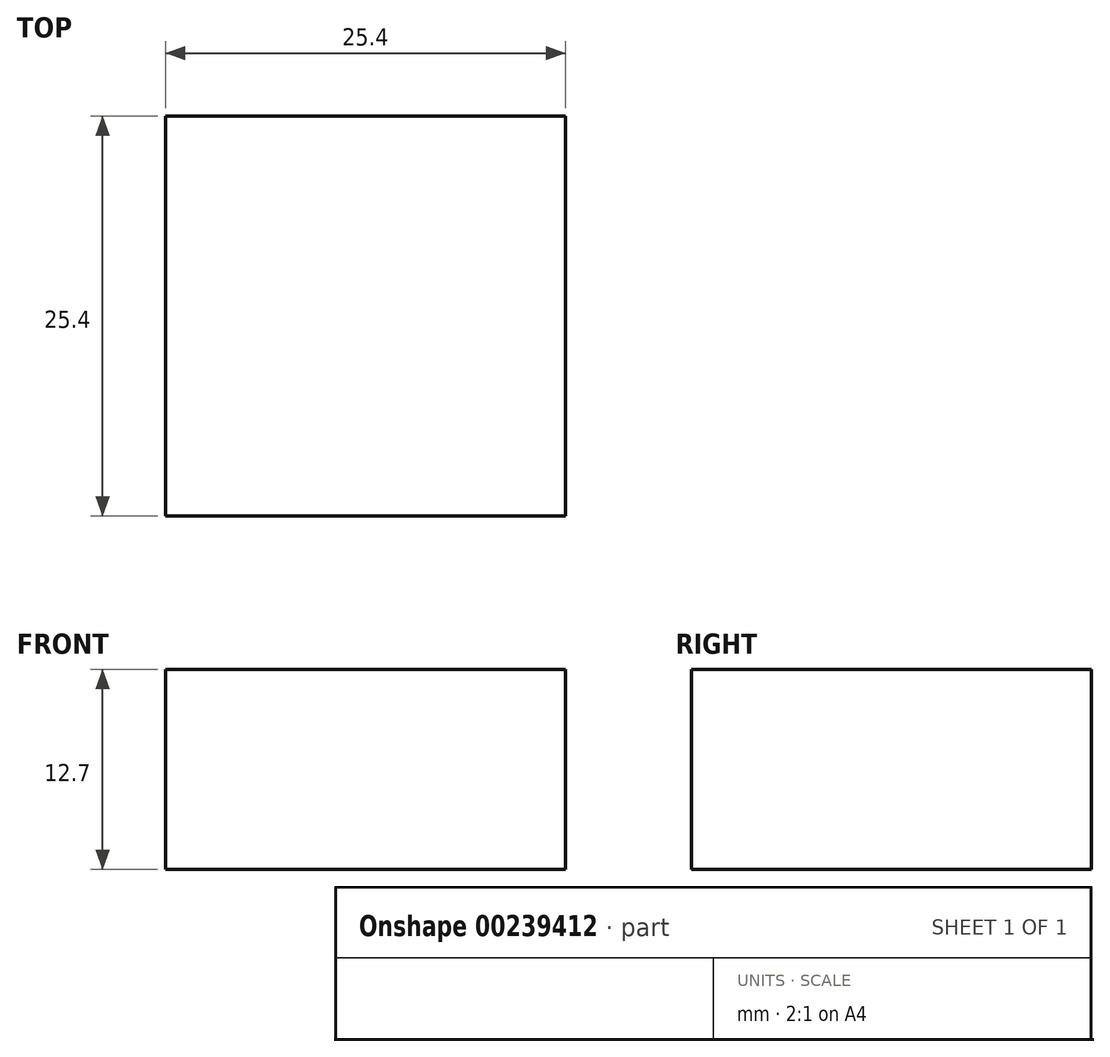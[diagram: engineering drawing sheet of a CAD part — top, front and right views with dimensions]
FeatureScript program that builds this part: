
annotation { "Feature Type Name" : "Feature", "Feature Type Description" : "" }
export const myFeature = defineFeature(function(context is Context, id is Id, definition is map)
    precondition{}
    {
        {
            var Q0;
            Q0=qCreatedBy(makeId("Front.planeOp"),FACE);
            var sketch = newSketch(context, id + "F0", { "sketchPlane" : qUnion([Q0])});
            skLineSegment(sketch, "E0.bottom", {"start": v(25.4, 12.7) * mm, "end": v(0, 12.7) * mm});
            skLineSegment(sketch, "E0.top", {"start": v(25.4, 0) * mm, "end": v(0, 0) * mm});
            skLineSegment(sketch, "E0.left", {"start": v(25.4, 12.7) * mm, "end": v(25.4, 0) * mm});
            skLineSegment(sketch, "E0.right", {"start": v(0, 12.7) * mm, "end": v(0, 0) * mm});
            skLineSegment(sketch, "E1", {"start": v(0, 0) * mm, "end": v(-92.48, 0) * mm, "construction": true});
            skLineSegment(sketch, "E2", {"start": v(0, 0) * mm, "end": v(0, 56.88) * mm, "construction": true});
            skSolve(sketch);
        }
        {
            var Q0;
            Q0=makeQuery(id+"F0.imprint","IMPRINT",FACE,{"disambiguationData":[TD([[makeQuery(id+"F0.imprint","IMPRINT",EDGE,{"derivedFrom":sQuery(id+"F0.wireOp",EDGE,"E0.bottom")}),1.0]])]});
            extrude(context, id + "F1", {"entities" : qUnion([Q0]), "depth" : 25.4 * mm});
        }
    });
